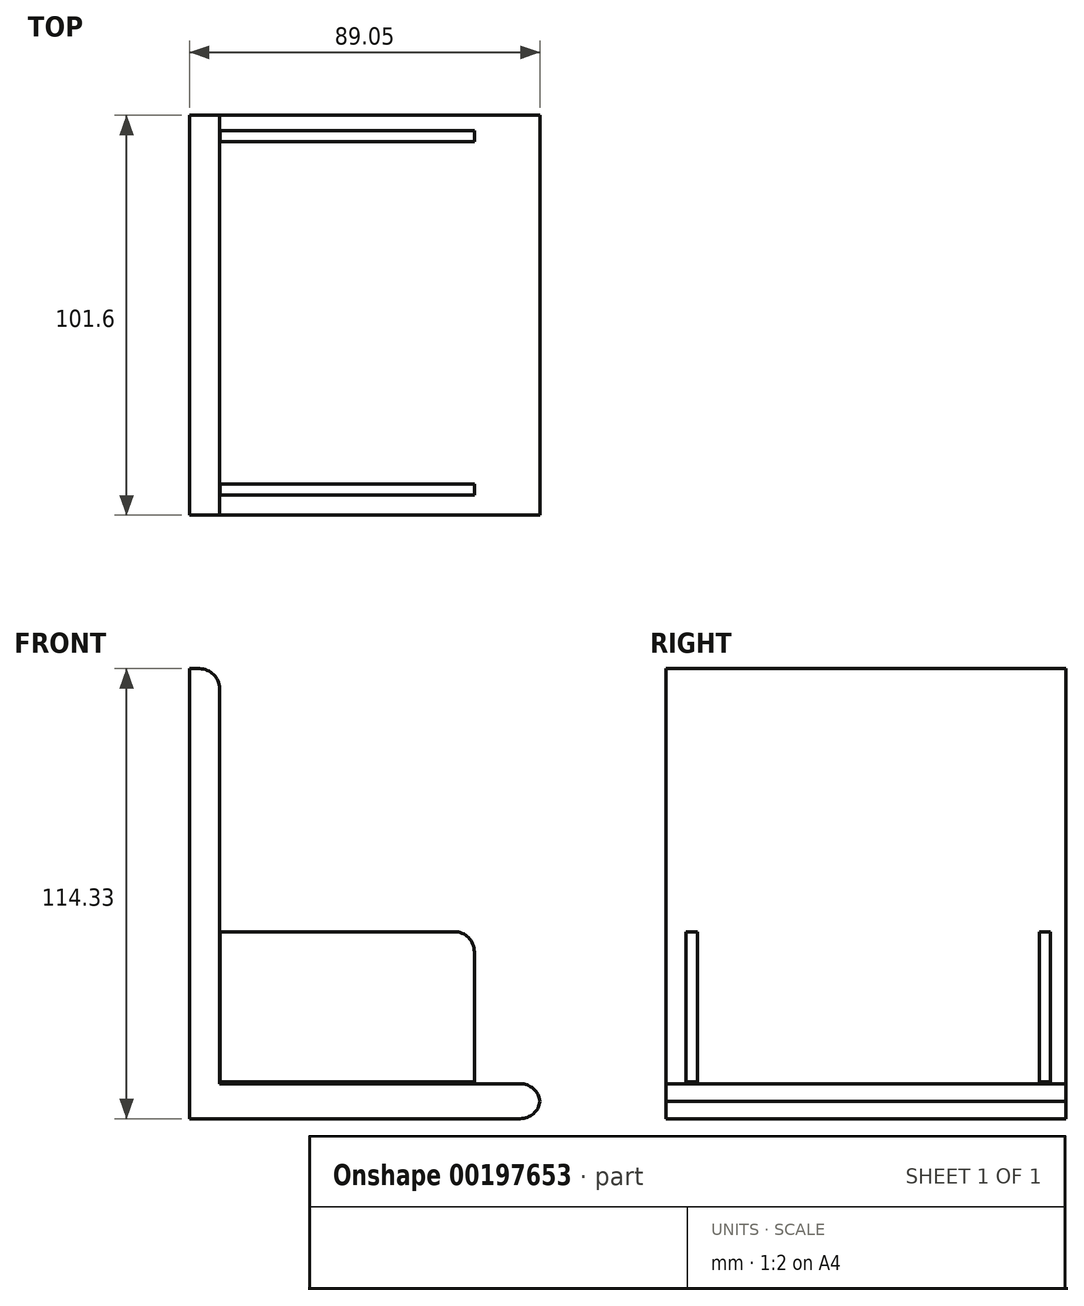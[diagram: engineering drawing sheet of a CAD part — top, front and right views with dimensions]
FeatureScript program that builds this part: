
annotation { "Feature Type Name" : "Feature", "Feature Type Description" : "" }
export const myFeature = defineFeature(function(context is Context, id is Id, definition is map)
    precondition{}
    {
        {
            var Q0;
            Q0=qCreatedBy(makeId("Front.planeOp"),FACE);
            var sketch = newSketch(context, id + "F0", { "sketchPlane" : qUnion([Q0])});
            skLineSegment(sketch, "E0.bottom", {"start": v(-53.72, 66.84) * mm, "end": v(-46.1, 66.84) * mm});
            skPoint(sketch, "E1.2.internal.snap0", {"position": v(10.96, -47.49) * mm});
            skLineSegment(sketch, "E2", {"start": v(-53.72, -47.49) * mm, "end": v(-46.2, -47.49) * mm});
            skLineSegment(sketch, "E3", {"start": v(-53.72, 66.84) * mm, "end": v(-53.72, -47.49) * mm});
            skLineSegment(sketch, "E4", {"start": v(-46.1, 66.84) * mm, "end": v(-46.1, -38.62) * mm});
            skLineSegment(sketch, "E5", {"start": v(35.37, -47.49) * mm, "end": v(35.37, -38.62) * mm});
            skLineSegment(sketch, "E6", {"start": v(35.37, -38.62) * mm, "end": v(-46.1, -38.62) * mm});
            skLineSegment(sketch, "E7", {"start": v(35.37, -47.49) * mm, "end": v(-46.2, -47.49) * mm});
            skSolve(sketch);
        }
        {
            var Q0;
            Q0=makeQuery(id+"F0.imprint","IMPRINT",FACE,{"disambiguationData":[TD([[makeQuery(id+"F0.imprint","IMPRINT",EDGE,{"derivedFrom":sQuery(id+"F0.wireOp",EDGE,"E0.bottom")}),-1.0]])]});
            extrude(context, id + "F1", {"entities" : qUnion([Q0]), "endBound" : BoundingType.SYMMETRIC, "depth" : 101.6 * mm});
        }
        {
            var Q0;
            Q0=qCreatedBy(makeId("Top.planeOp"),FACE);
            var sketch = newSketch(context, id + "F2", { "sketchPlane" : qUnion([Q0])});
            skLineSegment(sketch, "E8", {"start": v(-46, -45.67) * mm, "end": v(18.63, -45.67) * mm});
            skLineSegment(sketch, "E9", {"start": v(18.63, -45.67) * mm, "end": v(18.63, -42.84) * mm});
            skLineSegment(sketch, "E10", {"start": v(18.63, -42.84) * mm, "end": v(-46, -42.84) * mm});
            skLineSegment(sketch, "E11", {"start": v(-46, -42.84) * mm, "end": v(-46, -45.67) * mm});
            skLineSegment(sketch, "E12", {"start": v(-46, 46.91) * mm, "end": v(18.63, 46.91) * mm});
            skLineSegment(sketch, "E13", {"start": v(18.63, 46.91) * mm, "end": v(18.63, 44.08) * mm});
            skLineSegment(sketch, "E14", {"start": v(18.63, 44.08) * mm, "end": v(-46, 44.08) * mm});
            skLineSegment(sketch, "E15", {"start": v(-46, 44.08) * mm, "end": v(-46, 46.91) * mm});
            skSolve(sketch);
        }
        {
            var Q0;
            Q0=makeQuery(id+"F2.imprint","IMPRINT",FACE,{"disambiguationData":[TD([[makeQuery(id+"F2.imprint","IMPRINT",EDGE,{"derivedFrom":sQuery(id+"F2.wireOp",EDGE,"E12")}),-1.0]])]});
            var Q1;
            Q1=makeQuery(id+"F2.imprint","IMPRINT",FACE,{"disambiguationData":[TD([[makeQuery(id+"F2.imprint","IMPRINT",EDGE,{"derivedFrom":sQuery(id+"F2.wireOp",EDGE,"E8")}),1.0]])]});
            extrude(context, id + "F3", {"entities" : qUnion([Q0, Q1]), "oppositeDirection" : true, "depth" : 38.1 * mm});
        }
        {
            var Q0;
            Q0=makeQuery(id+"F1.opExtrude","SWEPT_EDGE",EDGE,{"disambiguationData":[OSD([sQuery(id+"F0.wireOp",EDGE,"E5"),sQuery(id+"F0.wireOp",EDGE,"E6")])]});
            var Q1;
            Q1=makeQuery(id+"F1.opExtrude","SWEPT_EDGE",EDGE,{"disambiguationData":[OSD([sQuery(id+"F0.wireOp",EDGE,"E5"),sQuery(id+"F0.wireOp",EDGE,"E7")])]});
            var Q2;
            Q2=makeQuery(id+"F1.opExtrude","SWEPT_EDGE",EDGE,{"disambiguationData":[OSD([sQuery(id+"F0.wireOp",EDGE,"E0.bottom"),sQuery(id+"F0.wireOp",EDGE,"E4")])]});
            var Q3;
            Q3=makeQuery(id+"F3.opExtrude","CAP_EDGE",EDGE,{"disambiguationData":[OSD([sQuery(id+"F2.wireOp",EDGE,"E13")])],"isStart":true});
            var Q4;
            Q4=makeQuery(id+"F3.opExtrude","CAP_EDGE",EDGE,{"disambiguationData":[OSD([sQuery(id+"F2.wireOp",EDGE,"E9")])],"isStart":true});
            fillet(context, id + "F4", {"entities" : qUnion([Q0, Q1, Q2, Q3, Q4]), "radius" : 5.08 * mm, "tangentPropagation" : true, "allowEdgeOverflow" : false});
        }
    });
